# Revit family: 315L Indoor Commercial Gas Storage Water Heater ,m,mn
name_source: partatom
category: Mechanical Equipment
revit_build: Autodesk Revit LT 2017 (Build: 20160225_1515(x64)
units: mm (PartAtom-declared; Revit-internal decimal feet)

## family parameters
Always vertical = Yes
Cut with Voids When Loaded = No
Part Type = Normal
Room Calculation Point = No
Round Connector Dimension = Use Diameter
Shared = No
Work Plane-Based = No

## types (1)
- Indoor
    Cold Water Inlet  connector description = Cold Water Inlet  connector description: Male threaded connector R1-1/4"(DN32)
    Exhaust Air pipe connector description = 80-125mm coaxial air connector
    Exhaust Air pipe connector system classification = Exhaust Air
    Exhaust Air pipe diameter = 130 mm
    Gas Inlet connector description = Gas Inlet connector description:Male threaded connector R¾”(DN20)
    Hot Water Outlet connector description = Hot Water Outlet connector: Male threaded connector R1-1/4"(DN32)
    No. of power supply point required = 1
    Nominal depth = 916mm
    Nominal gas consumption (MJ/h) = 205
    Nominal height = 1760mm
    Nominal width = 619mm
    Optional Cold Water Inlet connector description = Optional Cold Water Inlet connector: Male threaded connector R1-1/4"(DN32)
    Product SKU Dux brand = D12813FN/LTK
    Product SKU Thermann brand = T12813FN/LTK
    Product description = 315L Indoor Commercial Gas Storage Water Heater
    Supply Air/Air Inlet connector classification = Supply Air
    Supply Air/Air Inlet pipe connector description = 80-125mm coaxial air connector
    Supply Air/Air Inlet pipe diameter = 80 mm
    Total Maximum  power requirement(Watts) = 245
    Weight (Kg) = 139

## geometry (parser evidence)
native form markers: Sweep x2
no freeform markers — native parametric forms only
